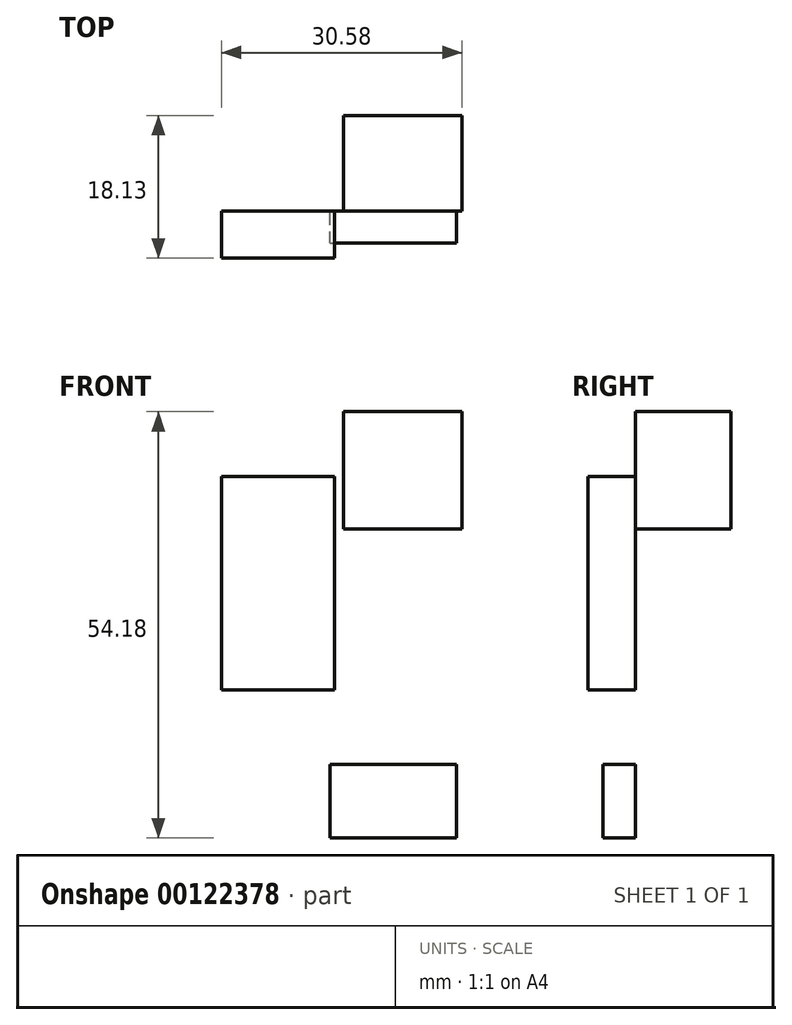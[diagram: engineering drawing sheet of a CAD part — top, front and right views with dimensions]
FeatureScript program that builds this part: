
annotation { "Feature Type Name" : "Feature", "Feature Type Description" : "" }
export const myFeature = defineFeature(function(context is Context, id is Id, definition is map)
    precondition{}
    {
        {
            var Q0;
            Q0=qCreatedBy(makeId("Front.planeOp"),FACE);
            var sketch = newSketch(context, id + "F0", { "sketchPlane" : qUnion([Q0])});
            skLineSegment(sketch, "E0.bottom", {"start": v(0, -22.2) * mm, "end": v(-13.68, -22.2) * mm});
            skLineSegment(sketch, "E0.top", {"start": v(0, -1.12) * mm, "end": v(-13.68, -1.12) * mm});
            skLineSegment(sketch, "E0.left", {"start": v(0, -22.2) * mm, "end": v(0, -1.12) * mm});
            skLineSegment(sketch, "E0.right", {"start": v(-13.68, -22.2) * mm, "end": v(-13.68, -1.12) * mm});
            skLineSegment(sketch, "E1.bottom", {"start": v(-15.36, -1.12) * mm, "end": v(1.68, -1.12) * mm});
            skLineSegment(sketch, "E1.top", {"start": v(-15.36, 14.52) * mm, "end": v(1.68, 14.52) * mm});
            skLineSegment(sketch, "E1.left", {"start": v(-15.36, -1.12) * mm, "end": v(-15.36, 14.52) * mm});
            skLineSegment(sketch, "E1.right", {"start": v(1.68, -1.12) * mm, "end": v(1.68, 14.52) * mm});
            skLineSegment(sketch, "E2.bottom", {"start": v(-14.94, -22.2) * mm, "end": v(0, -22.2) * mm});
            skLineSegment(sketch, "E2.left", {"start": v(-14.94, -22.2) * mm, "end": v(-14.94, -31.56) * mm});
            skLineSegment(sketch, "E3", {"start": v(-14.94, -31.56) * mm, "end": v(1.12, -31.56) * mm});
            skLineSegment(sketch, "E4", {"start": v(1.12, -31.56) * mm, "end": v(1.12, -22.2) * mm});
            skLineSegment(sketch, "E5", {"start": v(0, -22.2) * mm, "end": v(1.12, -22.2) * mm});
            skSolve(sketch);
        }
        {
            var Q0;
            {var subQ0=sQuery(id+"F0.wireOp",EDGE,"E2.left");Q0=makeQuery(id+"F0.imprint","IMPRINT",FACE,{"disambiguationData":[TD([[makeQuery(id+"F0.imprint","IMPRINT",EDGE,{"derivedFrom":subQ0}),1.0]])]});}
            extrude(context, id + "F1", {"entities" : qUnion([Q0]), "depth" : 4.1 * mm});
        }
        {
            var Q0;
            Q0=qCreatedBy(makeId("Front.planeOp"),FACE);
            var sketch = newSketch(context, id + "F2", { "sketchPlane" : qUnion([Q0])});
            skLineSegment(sketch, "E6.bottom", {"start": v(-13.27, 7.68) * mm, "end": v(1.82, 7.68) * mm});
            skLineSegment(sketch, "E6.top", {"start": v(-13.27, 22.62) * mm, "end": v(1.82, 22.62) * mm});
            skLineSegment(sketch, "E6.left", {"start": v(-13.27, 7.68) * mm, "end": v(-13.27, 22.62) * mm});
            skLineSegment(sketch, "E6.right", {"start": v(1.82, 7.68) * mm, "end": v(1.82, 22.62) * mm});
            skSolve(sketch);
        }
        {
            var Q0;
            Q0=qCreatedBy(makeId("Front.planeOp"),FACE);
            var sketch = newSketch(context, id + "F3", { "sketchPlane" : qUnion([Q0])});
            skLineSegment(sketch, "E7.bottom", {"start": v(-28.76, 14.38) * mm, "end": v(-14.38, 14.38) * mm});
            skLineSegment(sketch, "E7.top", {"start": v(-28.76, -12.7) * mm, "end": v(-14.38, -12.7) * mm});
            skLineSegment(sketch, "E7.left", {"start": v(-28.76, 14.38) * mm, "end": v(-28.76, -12.7) * mm});
            skLineSegment(sketch, "E7.right", {"start": v(-14.38, 14.38) * mm, "end": v(-14.38, -12.7) * mm});
            skSolve(sketch);
        }
        {
            var Q0;
            Q0=makeQuery(id+"F2.imprint","IMPRINT",FACE,{"disambiguationData":[TD([[makeQuery(id+"F2.imprint","IMPRINT",EDGE,{"derivedFrom":sQuery(id+"F2.wireOp",EDGE,"E6.bottom")}),1.0]])]});
            extrude(context, id + "F4", {"entities" : qUnion([Q0]), "oppositeDirection" : true, "depth" : 12.14 * mm});
        }
        {
            var Q0;
            Q0=makeQuery(id+"F3.imprint","IMPRINT",FACE,{"disambiguationData":[TD([[makeQuery(id+"F3.imprint","IMPRINT",EDGE,{"derivedFrom":sQuery(id+"F3.wireOp",EDGE,"E7.bottom")}),-1.0]])]});
            extrude(context, id + "F5", {"entities" : qUnion([Q0]), "depth" : 6 * mm});
        }
        {
            var Q0;
            Q0=qCreatedBy(makeId("Front.planeOp"),FACE);
            var sketch = newSketch(context, id + "F6", { "sketchPlane" : qUnion([Q0])});
            skLineSegment(sketch, "E8.bottom", {"start": v(-1.54, -24.16) * mm, "end": v(-4.75, -24.16) * mm});
            skLineSegment(sketch, "E8.top", {"start": v(-1.54, -27.23) * mm, "end": v(-4.75, -27.23) * mm});
            skLineSegment(sketch, "E8.left", {"start": v(-1.54, -24.16) * mm, "end": v(-1.54, -27.23) * mm});
            skLineSegment(sketch, "E8.right", {"start": v(-4.75, -24.16) * mm, "end": v(-4.75, -27.23) * mm});
            skSolve(sketch);
        }
        {
            var Q0;
            Q0=makeQuery(id+"F6.imprint","IMPRINT",FACE,{"disambiguationData":[TD([[makeQuery(id+"F6.imprint","IMPRINT",EDGE,{"derivedFrom":sQuery(id+"F6.wireOp",EDGE,"E8.bottom")}),1.0]])]});
            extrude(context, id + "F7", {"entities" : qUnion([Q0]), "operationType" : NewBodyOperationType.ADD, "depth" : 4.04 * mm});
        }
    });
